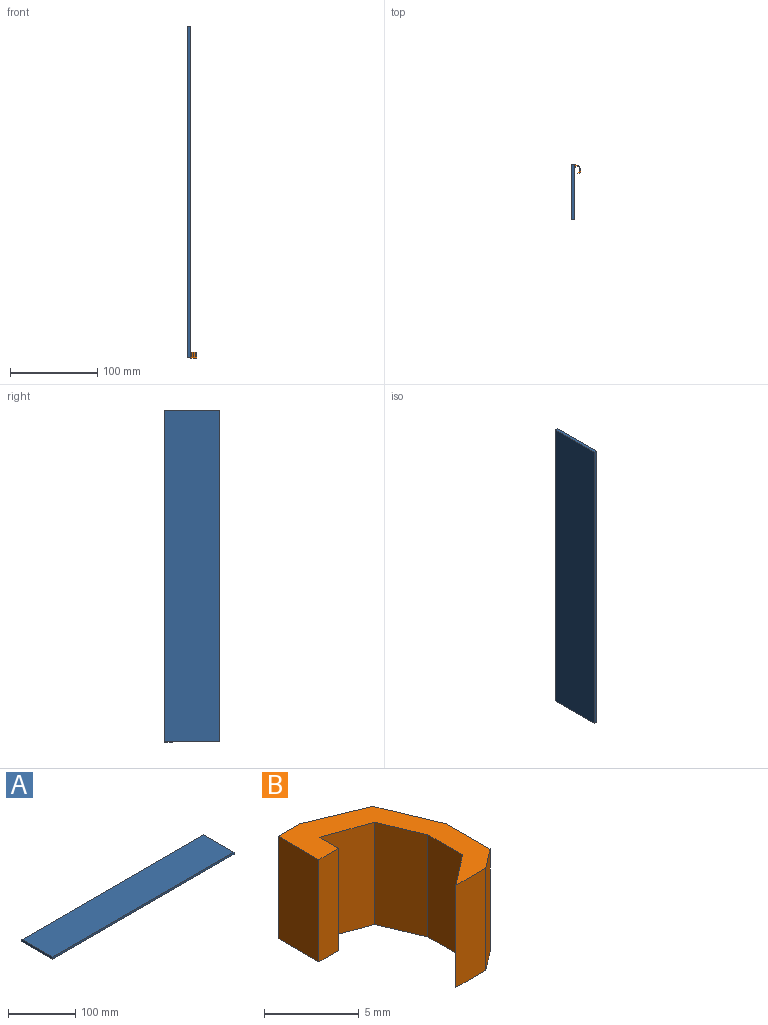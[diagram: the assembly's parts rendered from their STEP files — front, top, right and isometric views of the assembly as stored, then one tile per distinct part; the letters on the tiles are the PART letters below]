
ASSEMBLY  parts=2 mates=1
PART A: 6 faces, bbox 381x63.5x3.8 mm
  f0: plane 381x3.81mm, normal (0,1,0), area 1451.6mm2, adj f1,f3,f4,f5
  f1: plane 63.5x3.81mm, normal (-1,0,0), area 241.9mm2, adj f0,f2,f4,f5
  f2: plane 381x3.81mm, normal (0,-1,0), area 1451.6mm2, adj f1,f3,f4,f5
  f3: plane 63.5x3.81mm, normal (1,0,0), area 241.9mm2, adj f0,f2,f4,f5
  f4: plane 381x63.5mm, normal (0,0,1), area 24193.5mm2, adj f0,f1,f2,f3
  f5: plane 381x63.5mm, normal (0,0,-1), area 24193.5mm2, adj f0,f1,f2,f3
PART B: 15 faces, bbox 7.1x9.8x6.6 mm
  f0: plane 6.6x3.24mm, normal (1,0,0), area 21.4mm2, adj f1,f12,f13,f14
  f1: plane 6.6x3.88mm, normal (0.92,0.38,0), area 27.8mm2, adj f0,f2,f13,f14
  f2: plane 6.6x3.88mm, normal (0.38,0.92,0), area 27.8mm2, adj f1,f3,f13,f14
  f3: plane 6.6x1.59mm, normal (0,1,0), area 10.5mm2, adj f2,f4,f13,f14
  f4: plane 6.6x3.05mm, normal (-1,0,0), area 20.1mm2, adj f3,f5,f13,f14
  f5: plane 6.6x1.48mm, normal (0,-1,0), area 9.8mm2, adj f4,f6,f13,f14
  f6: plane 6.6x1.43mm, normal (1,0,0), area 9.5mm2, adj f5,f7,f13,f14
  f7: plane 6.6x3.02mm, normal (-0.34,-0.94,0), area 21.2mm2, adj f6,f8,f13,f14
  f8: plane 6.6x2.81mm, normal (-0.92,-0.39,0), area 20.1mm2, adj f7,f9,f13,f14
  f9: plane 6.6x2.6mm, normal (-1,0,0), area 17.2mm2, adj f8,f10,f13,f14
  f10: plane 6.6x2.23mm, normal (-0.61,0.79,0), area 18.6mm2, adj f9,f11,f13,f14
  f11: plane 6.6x2.23mm, normal (0,-1,0), area 14.7mm2, adj f10,f12,f13,f14
  f12: plane 6.6x1.4mm, normal (0.61,-0.79,0), area 11.7mm2, adj f0,f11,f13,f14
  f13: plane 9.82x7.09mm, normal (0,0,1), area 21.9mm2, adj f0,f1,f2,f3,f4,f5,f6,f7
  f14: plane 9.82x7.09mm, normal (0,0,-1), area 21.9mm2, adj f0,f1,f2,f3,f4,f5,f6,f7
PLACE A rot(axis=(0,-1,0),90deg) t=(47.88,-24.09,50.16)mm
PLACE B t=(89.02,19.18,-3.13)mm
MATE fastened A.f5 <-> B.f4  axis (1,0,0) through (47.88,57.41,-3.13)mm
